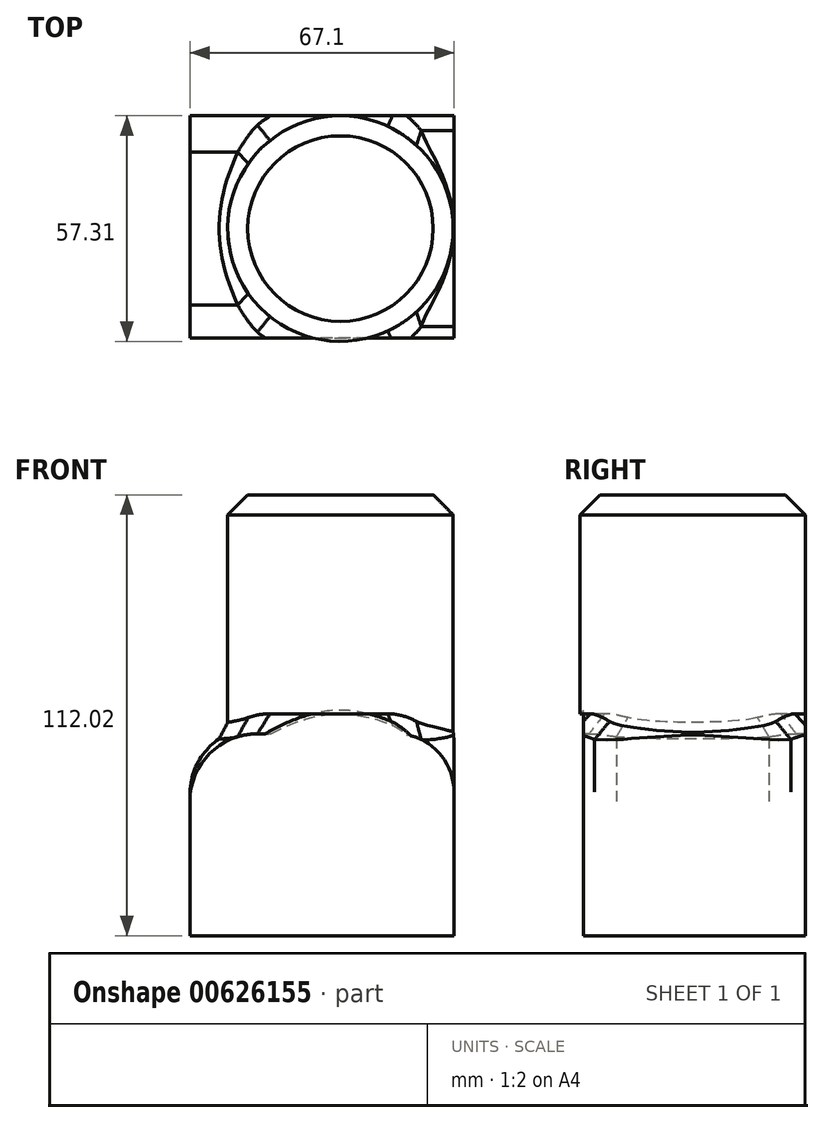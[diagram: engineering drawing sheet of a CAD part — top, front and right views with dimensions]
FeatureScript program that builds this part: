
annotation { "Feature Type Name" : "Feature", "Feature Type Description" : "" }
export const myFeature = defineFeature(function(context is Context, id is Id, definition is map)
    precondition{}
    {
        {
            var Q0;
            Q0=qCreatedBy(makeId("Top.planeOp"),FACE);
            var sketch = newSketch(context, id + "F0", { "sketchPlane" : qUnion([Q0])});
            skCircle(sketch, "E0", {"center": v(0, 0) * mm, "radius": 28.64 * mm});
            skSolve(sketch);
        }
        {
            var Q0;
            Q0=makeQuery(id+"F0.imprint","IMPRINT",FACE,{"disambiguationData":[TD([[makeQuery(id+"F0.imprint","IMPRINT",EDGE,{"derivedFrom":sQuery(id+"F0.wireOp",EDGE,"E0")}),1.0]])]});
            extrude(context, id + "F1", {"entities" : qUnion([Q0]), "depth" : 60.7 * mm, "offsetDistance" : 25.4 * mm});
        }
        {
            var Q0;
            Q0=qCreatedBy(makeId("Top.planeOp"),FACE);
            var sketch = newSketch(context, id + "F2", { "sketchPlane" : qUnion([Q0])});
            skLineSegment(sketch, "E1.bottom", {"start": v(-38.25, -27.75) * mm, "end": v(28.85, -27.75) * mm});
            skLineSegment(sketch, "E1.top", {"start": v(-38.25, 28.67) * mm, "end": v(28.85, 28.67) * mm});
            skLineSegment(sketch, "E1.left", {"start": v(-38.25, -27.75) * mm, "end": v(-38.25, 28.67) * mm});
            skLineSegment(sketch, "E1.right", {"start": v(28.85, -27.75) * mm, "end": v(28.85, 28.67) * mm});
            skSolve(sketch);
        }
        {
            var Q0;
            Q0=makeQuery(id+"F2.imprint","IMPRINT",FACE,{"disambiguationData":[TD([[makeQuery(id+"F2.imprint","IMPRINT",EDGE,{"derivedFrom":sQuery(id+"F2.wireOp",EDGE,"E1.bottom")}),1.0]])]});
            extrude(context, id + "F3", {"entities" : qUnion([Q0]), "operationType" : NewBodyOperationType.ADD, "oppositeDirection" : true, "depth" : 51.3 * mm, "offsetDistance" : 25.4 * mm});
        }
        {
            var Q0;
            Q0=makeQuery(id+"F3.opExtrude","CAP_EDGE",EDGE,{"disambiguationData":[OSD([sQuery(id+"F2.wireOp",EDGE,"E1.right")])],"isStart":true});
            fillet(context, id + "F4", {"entities" : qUnion([Q0]), "radius" : 14.72 * mm, "tangentPropagation" : true, "allowEdgeOverflow" : false});
        }
        {
            var Q0;
            Q0=makeQuery(id+"F3.opExtrude","CAP_EDGE",EDGE,{"disambiguationData":[OSD([sQuery(id+"F2.wireOp",EDGE,"E1.left")])],"isStart":true});
            fillet(context, id + "F5", {"entities" : qUnion([Q0]), "radius" : 17.17 * mm, "tangentPropagation" : true, "allowEdgeOverflow" : false});
        }
        {
            var Q0;
            Q0=makeQuery(id+"F1.opExtrude","CAP_EDGE",EDGE,{"disambiguationData":[OSD([sQuery(id+"F0.wireOp",EDGE,"E0")])],"isStart":false});
            var Q1;
            Q1=makeQuery(id+"F1.opExtrude","SWEPT_FACE",FACE,{"disambiguationData":[OSD([sQuery(id+"F0.wireOp",EDGE,"E0")])]});
            chamfer(context, id + "F6", {"entities" : qUnion([Q0, Q1]), "width" : 5.08 * mm, "tangentPropagation" : true});
        }
    });
